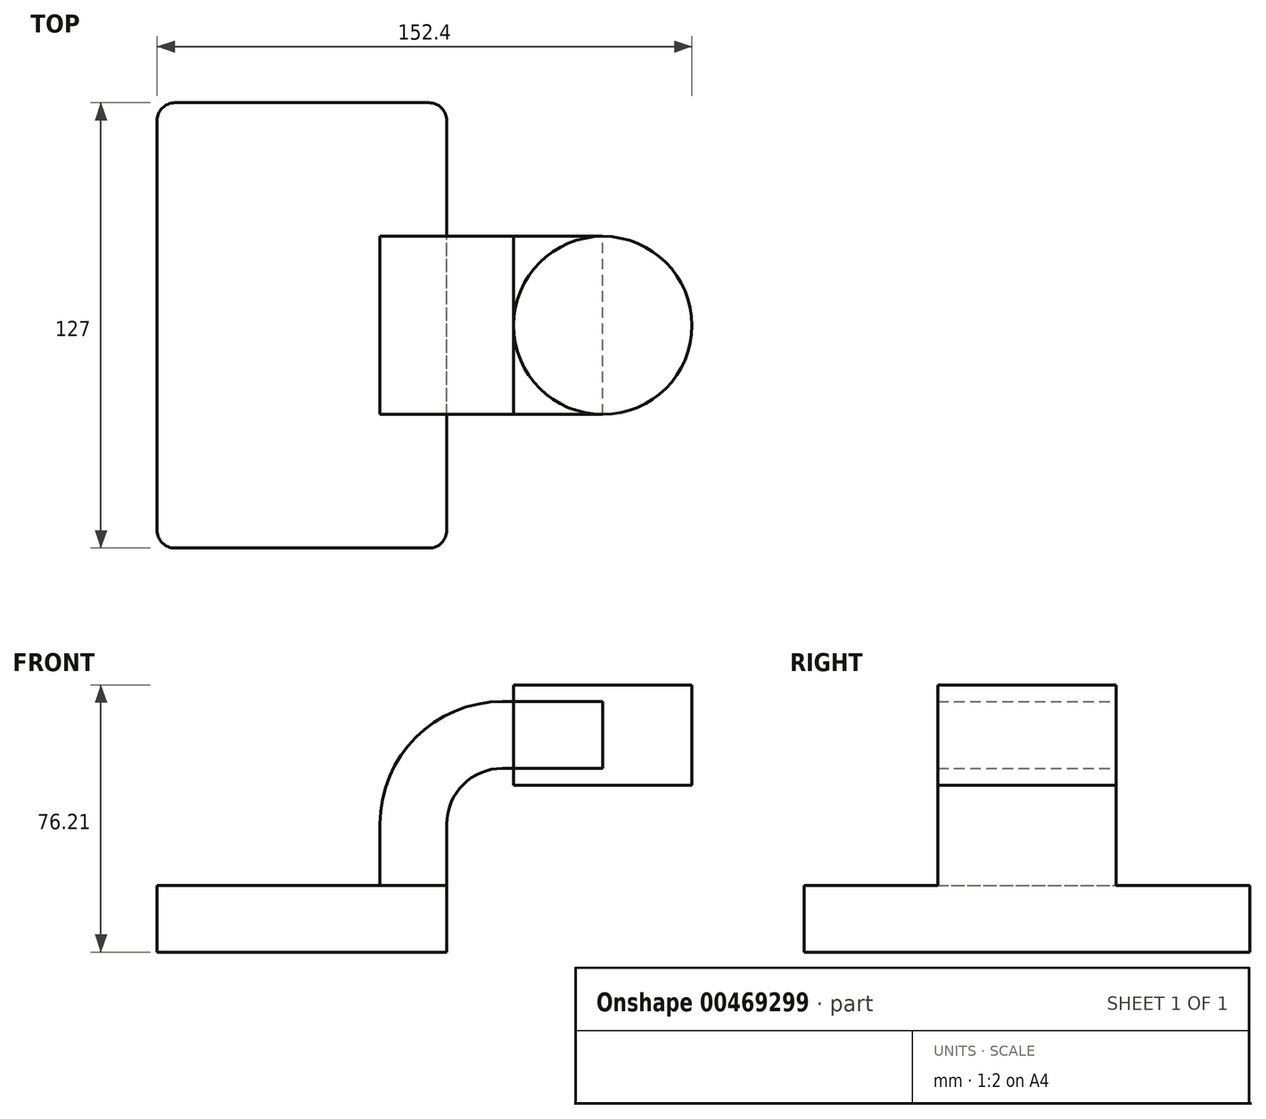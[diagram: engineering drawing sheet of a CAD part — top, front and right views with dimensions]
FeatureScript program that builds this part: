
annotation { "Feature Type Name" : "Feature", "Feature Type Description" : "" }
export const myFeature = defineFeature(function(context is Context, id is Id, definition is map)
    precondition{}
    {
        {
            var Q0;
            Q0=qCreatedBy(makeId("Front.planeOp"),FACE);
            var sketch = newSketch(context, id + "F0", { "sketchPlane" : qUnion([Q0])});
            skLineSegment(sketch, "E0.bottom", {"start": v(41.27, 9.52) * mm, "end": v(-41.28, 9.52) * mm});
            skLineSegment(sketch, "E0.top", {"start": v(41.28, -9.53) * mm, "end": v(-41.27, -9.53) * mm});
            skLineSegment(sketch, "E0.left", {"start": v(41.28, 9.52) * mm, "end": v(41.28, -9.53) * mm});
            skLineSegment(sketch, "E0.right", {"start": v(-41.27, 9.52) * mm, "end": v(-41.27, -9.53) * mm});
            skPoint(sketch, "E0.middle", {"position": v(0, 0) * mm});
            skLineSegment(sketch, "E1.bottom", {"start": v(111.13, 38.1) * mm, "end": v(60.33, 38.1) * mm});
            skLineSegment(sketch, "E1.top", {"start": v(111.13, 66.67) * mm, "end": v(60.33, 66.67) * mm});
            skLineSegment(sketch, "E1.left", {"start": v(111.13, 38.1) * mm, "end": v(111.13, 66.67) * mm});
            skLineSegment(sketch, "E1.right", {"start": v(60.33, 38.1) * mm, "end": v(60.33, 66.67) * mm});
            skPoint(sketch, "E1.middle", {"position": v(85.73, 52.39) * mm});
            skLineSegment(sketch, "E2", {"start": v(41.27, 9.52) * mm, "end": v(41.27, 27) * mm});
            skArc(sketch, "E3", {"start": v(41.28, 27) * mm, "mid": v(45.92, 38.23) * mm, "end": v(57.15, 42.88) * mm});
            skLineSegment(sketch, "E4", {"start": v(57.15, 42.88) * mm, "end": v(85.72, 42.88) * mm});
            skLineSegment(sketch, "E5.0", {"start": v(57.15, 61.93) * mm, "end": v(85.72, 61.93) * mm});
            skArc(sketch, "E5.1", {"start": v(22.23, 27) * mm, "mid": v(32.45, 51.7) * mm, "end": v(57.15, 61.93) * mm});
            skLineSegment(sketch, "E5.2", {"start": v(22.23, 9.52) * mm, "end": v(22.23, 27) * mm});
            skLineSegment(sketch, "E6", {"start": v(85.73, 38.1) * mm, "end": v(85.73, 66.67) * mm});
            skFitSpline(sketch, "E7", {"points": [v(-41.28, 9.52) * mm, v(57.15, 61.93) * mm], "startDerivative": vector(0.32, 87.64) * mm, "endDerivative": vector(129.3, -0.5) * mm});
            skSolve(sketch);
        }
        {
            var Q0;
            Q0=makeQuery(id+"F0.imprint","IMPRINT",FACE,{"disambiguationData":[TD([[makeQuery(id+"F0.imprint","IMPRINT",EDGE,{"derivedFrom":sQuery(id+"F0.wireOp",EDGE,"E0.top")}),-1.0]])]});
            extrude(context, id + "F1", {"entities" : qUnion([Q0]), "endBound" : BoundingType.SYMMETRIC, "depth" : 127 * mm});
        }
        {
            var Q0;
            {var subQ1=sQuery(id+"F0.wireOp",EDGE,"E2");Q0=makeQuery(id+"F0.imprint","IMPRINT",FACE,{"disambiguationData":[TD([[makeQuery(id+"F0.imprint","IMPRINT",EDGE,{"derivedFrom":subQ1}),1.0]])]});}
            extrude(context, id + "F2", {"entities" : qUnion([Q0]), "operationType" : NewBodyOperationType.ADD, "endBound" : BoundingType.SYMMETRIC, "depth" : 50.8 * mm});
        }
        {
            var Q0;
            Q0=makeQuery(id+"F0.imprint","IMPRINT",FACE,{"disambiguationData":[TD([[makeQuery(id+"F0.imprint","IMPRINT",EDGE,{"derivedFrom":sQuery(id+"F0.wireOp",EDGE,"E5.1")}),1.0]])]});
            extrude(context, id + "F3", {"entities" : qUnion([Q0]), "operationType" : NewBodyOperationType.ADD, "endBound" : BoundingType.SYMMETRIC, "depth" : 15.88 * mm});
        }
        {
            var Q0;
            {var subQ4=sQuery(id+"F0.wireOp",EDGE,"E1.left");Q0=makeQuery(id+"F0.imprint","IMPRINT",FACE,{"disambiguationData":[TD([[makeQuery(id+"F0.imprint","IMPRINT",EDGE,{"derivedFrom":subQ4}),1.0]])]});}
            var Q1;
            Q1=sQuery(id+"F0.wireOp",EDGE,"E6");
            revolve(context, id + "F4", {"operationType" : NewBodyOperationType.ADD, "entities" : qUnion([Q0]), "axis" : qUnion([Q1]), "revolveType" : RevolveType.FULL});
        }
        {
            var Q0;
            Q0=makeQuery(id+"F2.opExtrude","SWEPT_FACE",FACE,{"disambiguationData":[OSD([sQuery(id+"F0.wireOp",EDGE,"E1.right")])]});
            extrude(context, id + "F5", {"entities" : qUnion([Q0]), "depth" : 25.4 * mm});
        }
        {
            var Q0;
            Q0=makeQuery(id+"F1.opExtrude","CAP_EDGE",EDGE,{"disambiguationData":[OSD([sQuery(id+"F0.wireOp",EDGE,"E0.right")])],"isStart":false});
            var Q1;
            Q1=makeQuery(id+"F1.opExtrude","CAP_EDGE",EDGE,{"disambiguationData":[OSD([sQuery(id+"F0.wireOp",EDGE,"E0.left")])],"isStart":false});
            var Q2;
            Q2=makeQuery(id+"F1.opExtrude","CAP_EDGE",EDGE,{"disambiguationData":[OSD([sQuery(id+"F0.wireOp",EDGE,"E0.left")])],"isStart":true});
            var Q3;
            Q3=makeQuery(id+"F1.opExtrude","CAP_EDGE",EDGE,{"disambiguationData":[OSD([sQuery(id+"F0.wireOp",EDGE,"E0.right")])],"isStart":true});
            fillet(context, id + "F6", {"entities" : qUnion([Q0, Q1, Q2, Q3]), "radius" : 5.08 * mm, "tangentPropagation" : true, "allowEdgeOverflow" : false});
        }
    });
